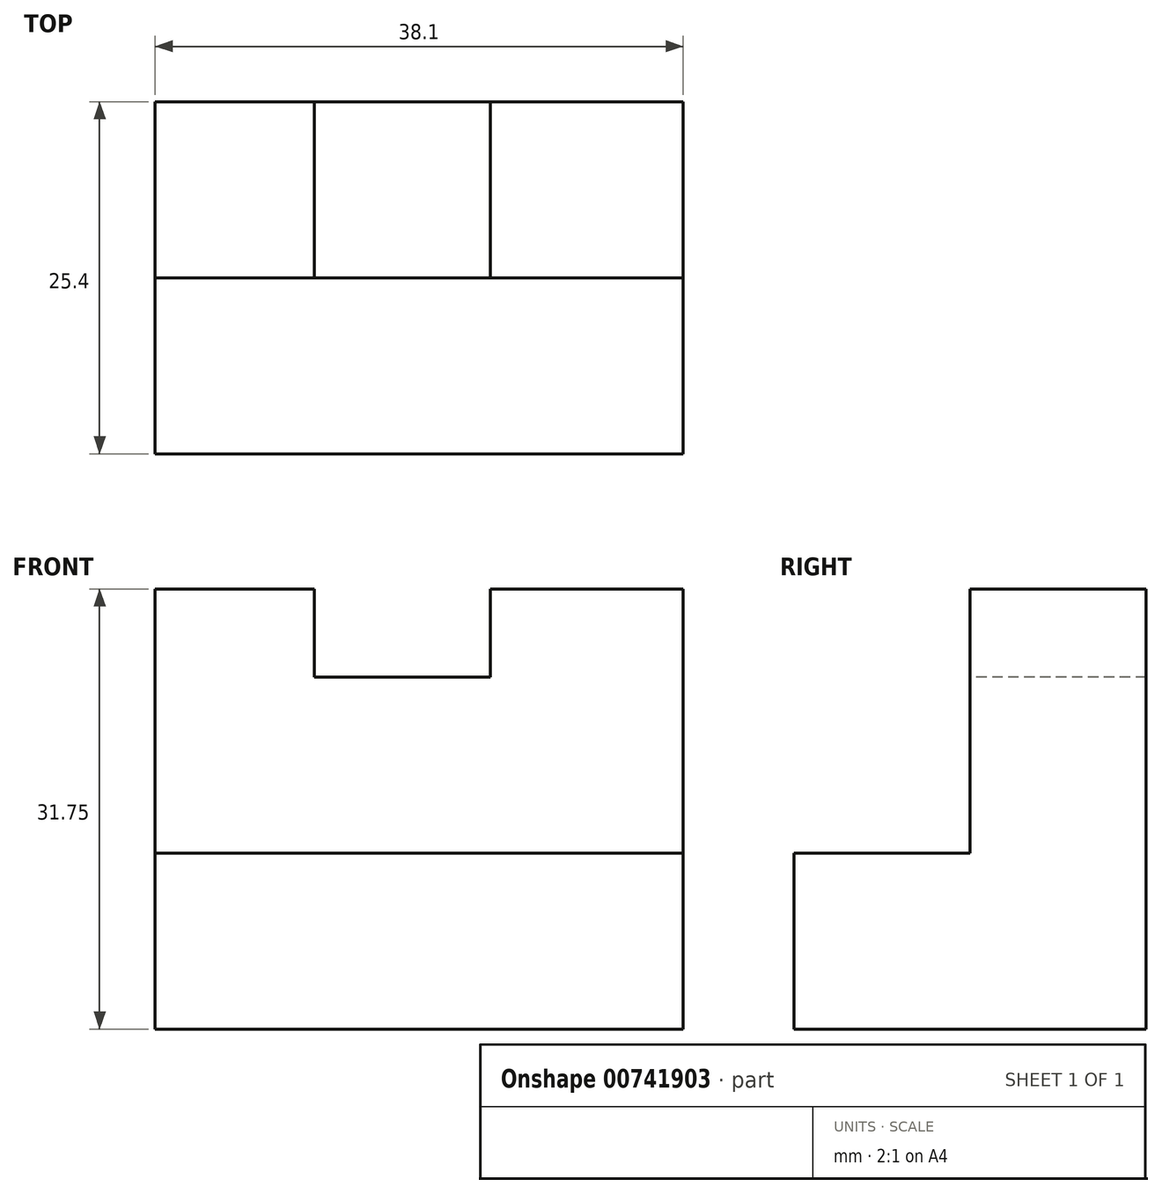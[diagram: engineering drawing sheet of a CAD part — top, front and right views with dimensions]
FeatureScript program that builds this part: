
annotation { "Feature Type Name" : "Feature", "Feature Type Description" : "" }
export const myFeature = defineFeature(function(context is Context, id is Id, definition is map)
    precondition{}
    {
        {
            var Q0;
            Q0=qCreatedBy(makeId("Right.planeOp"),FACE);
            var sketch = newSketch(context, id + "F0", { "sketchPlane" : qUnion([Q0])});
            skLineSegment(sketch, "E0", {"start": v(0, 31.75) * mm, "end": v(0, 0) * mm});
            skLineSegment(sketch, "E1", {"start": v(-25.4, 0) * mm, "end": v(-25.4, 12.7) * mm});
            skLineSegment(sketch, "E2", {"start": v(-25.4, 12.7) * mm, "end": v(-12.7, 12.7) * mm});
            skLineSegment(sketch, "E3", {"start": v(-12.7, 12.7) * mm, "end": v(-12.7, 31.75) * mm});
            skLineSegment(sketch, "E4", {"start": v(-12.7, 31.75) * mm, "end": v(0, 31.75) * mm});
            skLineSegment(sketch, "E5", {"start": v(-25.4, 0) * mm, "end": v(0, 0) * mm});
            skSolve(sketch);
        }
        {
            var Q0;
            Q0 = qSketchRegion(id + "F0", true);
            extrude(context, id + "F1", {"entities" : qUnion([Q0]), "depth" : 38.1 * mm, "offsetDistance" : 25.4 * mm});
        }
        {
            var Q0;
            Q0=makeQuery(id+"F1.opExtrude","SWEPT_FACE",FACE,{"disambiguationData":[OSD([sQuery(id+"F0.wireOp",EDGE,"E3")])]});
            var sketch = newSketch(context, id + "F2", { "sketchPlane" : qUnion([Q0])});
            skLineSegment(sketch, "E6", {"start": v(11.5, 31.75) * mm, "end": v(11.5, 25.4) * mm});
            skLineSegment(sketch, "E7", {"start": v(11.5, 25.4) * mm, "end": v(24.2, 25.4) * mm});
            skLineSegment(sketch, "E8", {"start": v(24.2, 25.4) * mm, "end": v(24.2, 31.75) * mm});
            skLineSegment(sketch, "E9", {"start": v(25.4, 31.27) * mm, "end": v(38.1, 31.75) * mm});
            skSolve(sketch);
        }
        {
            var Q0;
            {var subQ0=sQuery(id+"F2.wireOp",EDGE,"E6");Q0=makeQuery(id+"F2.imprint","IMPRINT",FACE,{"disambiguationData":[TD([[makeQuery(id+"F2.imprint","IMPRINT",EDGE,{"derivedFrom":subQ0}),1.0]])]});}
            extrude(context, id + "F3", {"entities" : qUnion([Q0]), "operationType" : NewBodyOperationType.REMOVE, "endBound" : BoundingType.THROUGH_ALL, "oppositeDirection" : true, "depth" : 25.4 * mm, "offsetDistance" : 25.4 * mm});
        }
    });
